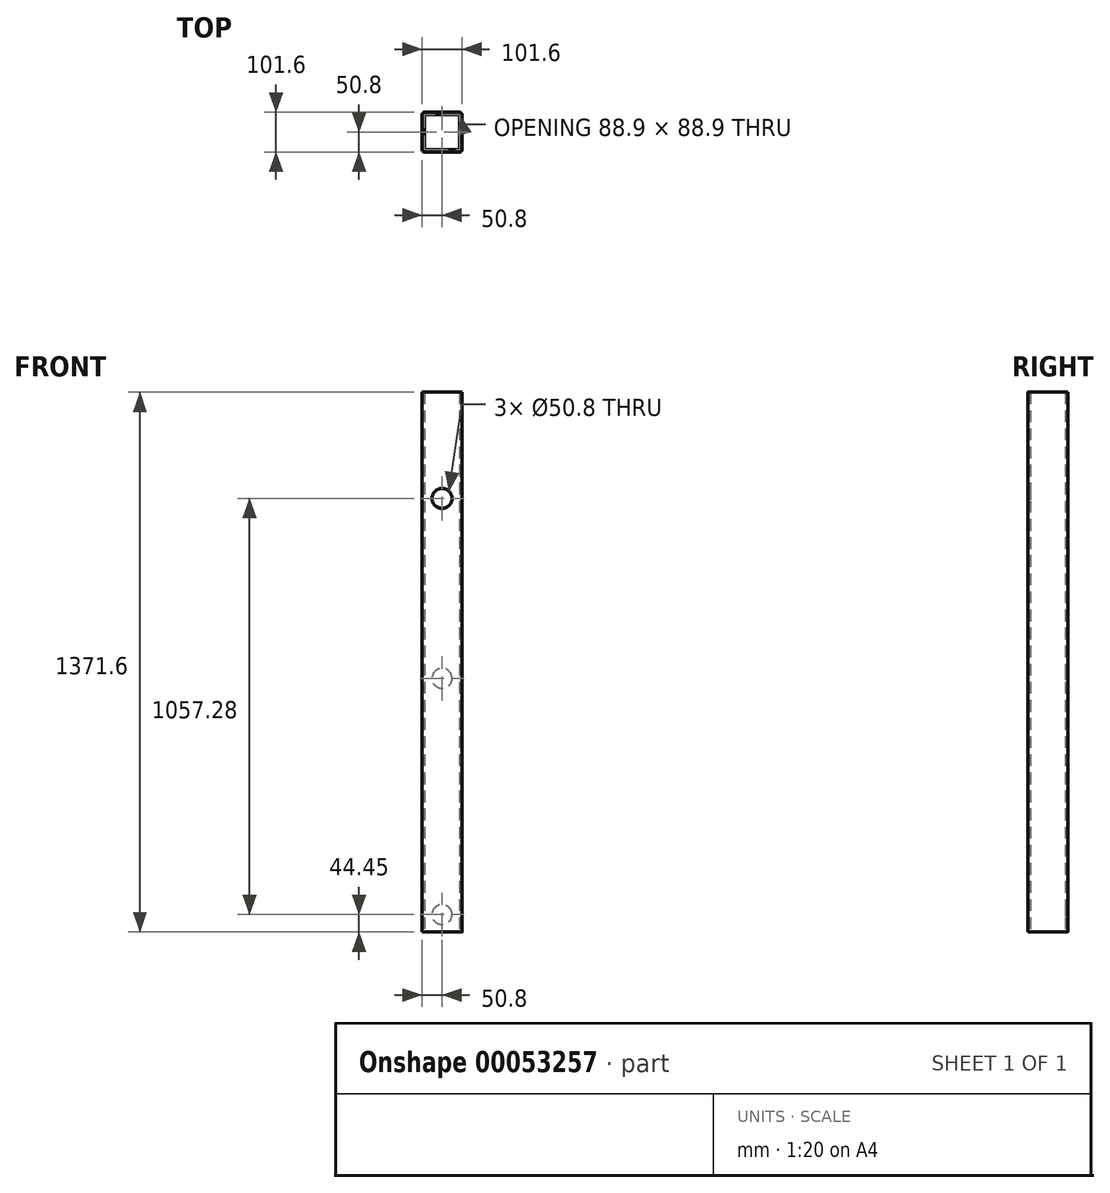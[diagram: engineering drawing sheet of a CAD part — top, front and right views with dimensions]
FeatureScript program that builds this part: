
annotation { "Feature Type Name" : "Feature", "Feature Type Description" : "" }
export const myFeature = defineFeature(function(context is Context, id is Id, definition is map)
    precondition{}
    {
        {
            var Q0;
            Q0=qCreatedBy(makeId("Top.planeOp"),FACE);
            var sketch = newSketch(context, id + "F0", { "sketchPlane" : qUnion([Q0])});
            skLineSegment(sketch, "E0.bottom", {"start": v(-44.45, 50.8) * mm, "end": v(44.45, 50.8) * mm});
            skLineSegment(sketch, "E0.top", {"start": v(-44.45, -50.8) * mm, "end": v(44.45, -50.8) * mm});
            skLineSegment(sketch, "E0.left", {"start": v(-50.8, 44.45) * mm, "end": v(-50.8, -44.45) * mm});
            skLineSegment(sketch, "E0.right", {"start": v(50.8, 44.45) * mm, "end": v(50.8, -44.45) * mm});
            skLineSegment(sketch, "E1.0", {"start": v(-41.28, 44.45) * mm, "end": v(41.28, 44.45) * mm});
            skLineSegment(sketch, "E2.0", {"start": v(-41.28, -44.45) * mm, "end": v(41.27, -44.45) * mm});
            skLineSegment(sketch, "E3.0", {"start": v(44.45, 41.28) * mm, "end": v(44.45, -41.28) * mm});
            skLineSegment(sketch, "E4.0", {"start": v(-44.45, 41.28) * mm, "end": v(-44.45, -41.28) * mm});
            skPoint(sketch, "E5.visualSharp", {"position": v(-50.8, -50.8) * mm});
            skArc(sketch, "E5.filletArc", {"start": v(-50.8, -44.45) * mm, "mid": v(-48.94, -48.94) * mm, "end": v(-44.45, -50.8) * mm});
            skArc(sketch, "E6.filletArc", {"start": v(-44.45, -41.28) * mm, "mid": v(-43.52, -43.52) * mm, "end": v(-41.28, -44.45) * mm});
            skPoint(sketch, "E7.visualSharp", {"position": v(50.8, -50.8) * mm});
            skArc(sketch, "E7.filletArc", {"start": v(44.45, -50.8) * mm, "mid": v(48.94, -48.94) * mm, "end": v(50.8, -44.45) * mm});
            skArc(sketch, "E8.filletArc", {"start": v(41.27, -44.45) * mm, "mid": v(43.52, -43.52) * mm, "end": v(44.45, -41.28) * mm});
            skPoint(sketch, "E9.visualSharp", {"position": v(50.8, 50.8) * mm});
            skArc(sketch, "E9.filletArc", {"start": v(50.8, 44.45) * mm, "mid": v(48.94, 48.94) * mm, "end": v(44.45, 50.8) * mm});
            skArc(sketch, "E10.filletArc", {"start": v(44.45, 41.28) * mm, "mid": v(43.52, 43.52) * mm, "end": v(41.28, 44.45) * mm});
            skPoint(sketch, "E11.visualSharp", {"position": v(-44.45, 44.45) * mm});
            skArc(sketch, "E11.filletArc", {"start": v(-41.28, 44.45) * mm, "mid": v(-43.52, 43.52) * mm, "end": v(-44.45, 41.28) * mm});
            skPoint(sketch, "E12.visualSharp", {"position": v(-50.8, 50.8) * mm});
            skArc(sketch, "E12.filletArc", {"start": v(-44.45, 50.8) * mm, "mid": v(-48.94, 48.94) * mm, "end": v(-50.8, 44.45) * mm});
            skSolve(sketch);
        }
        {
            var Q0;
            Q0=makeQuery(id+"F0.imprint","IMPRINT",FACE,{"disambiguationData":[TD([[makeQuery(id+"F0.imprint","IMPRINT",EDGE,{"derivedFrom":sQuery(id+"F0.wireOp",EDGE,"E0.bottom")}),-1.0]])]});
            extrude(context, id + "F1", {"entities" : qUnion([Q0]), "depth" : 1371.6 * mm});
        }
        {
            var Q0;
            Q0=makeQuery(id+"F1.opExtrude","SWEPT_FACE",FACE,{"disambiguationData":[OSD([sQuery(id+"F0.wireOp",EDGE,"E0.bottom")])]});
            var sketch = newSketch(context, id + "F2", { "sketchPlane" : qUnion([Q0])});
            skCircle(sketch, "E13", {"center": v(0, 44.45) * mm, "radius": 25.4 * mm});
            skCircle(sketch, "E14", {"center": v(0, 644.52) * mm, "radius": 25.4 * mm});
            skSolve(sketch);
        }
        {
            var Q0;
            Q0=makeQuery(id+"F2.imprint","IMPRINT",FACE,{"disambiguationData":[TD([[makeQuery(id+"F2.imprint","IMPRINT",EDGE,{"derivedFrom":sQuery(id+"F2.wireOp",EDGE,"E14")}),1.0]])]});
            var Q1;
            Q1=makeQuery(id+"F2.imprint","IMPRINT",FACE,{"disambiguationData":[TD([[makeQuery(id+"F2.imprint","IMPRINT",EDGE,{"derivedFrom":sQuery(id+"F2.wireOp",EDGE,"E13")}),1.0]])]});
            extrude(context, id + "F3", {"entities" : qUnion([Q0, Q1]), "operationType" : NewBodyOperationType.REMOVE, "endBound" : BoundingType.UP_TO_NEXT, "oppositeDirection" : true, "depth" : 25.4 * mm});
        }
        {
            var Q0;
            Q0=makeQuery(id+"F1.opExtrude","SWEPT_FACE",FACE,{"disambiguationData":[OSD([sQuery(id+"F0.wireOp",EDGE,"E0.top")])]});
            var sketch = newSketch(context, id + "F4", { "sketchPlane" : qUnion([Q0])});
            skCircle(sketch, "E15", {"center": v(0, 1101.73) * mm, "radius": 25.4 * mm});
            skSolve(sketch);
        }
        {
            var Q0;
            Q0=makeQuery(id+"F4.imprint","IMPRINT",FACE,{"disambiguationData":[TD([[makeQuery(id+"F4.imprint","IMPRINT",EDGE,{"derivedFrom":sQuery(id+"F4.wireOp",EDGE,"E15")}),1.0]])]});
            extrude(context, id + "F5", {"entities" : qUnion([Q0]), "operationType" : NewBodyOperationType.REMOVE, "endBound" : BoundingType.UP_TO_NEXT, "oppositeDirection" : true, "depth" : 25.4 * mm});
        }
    });
